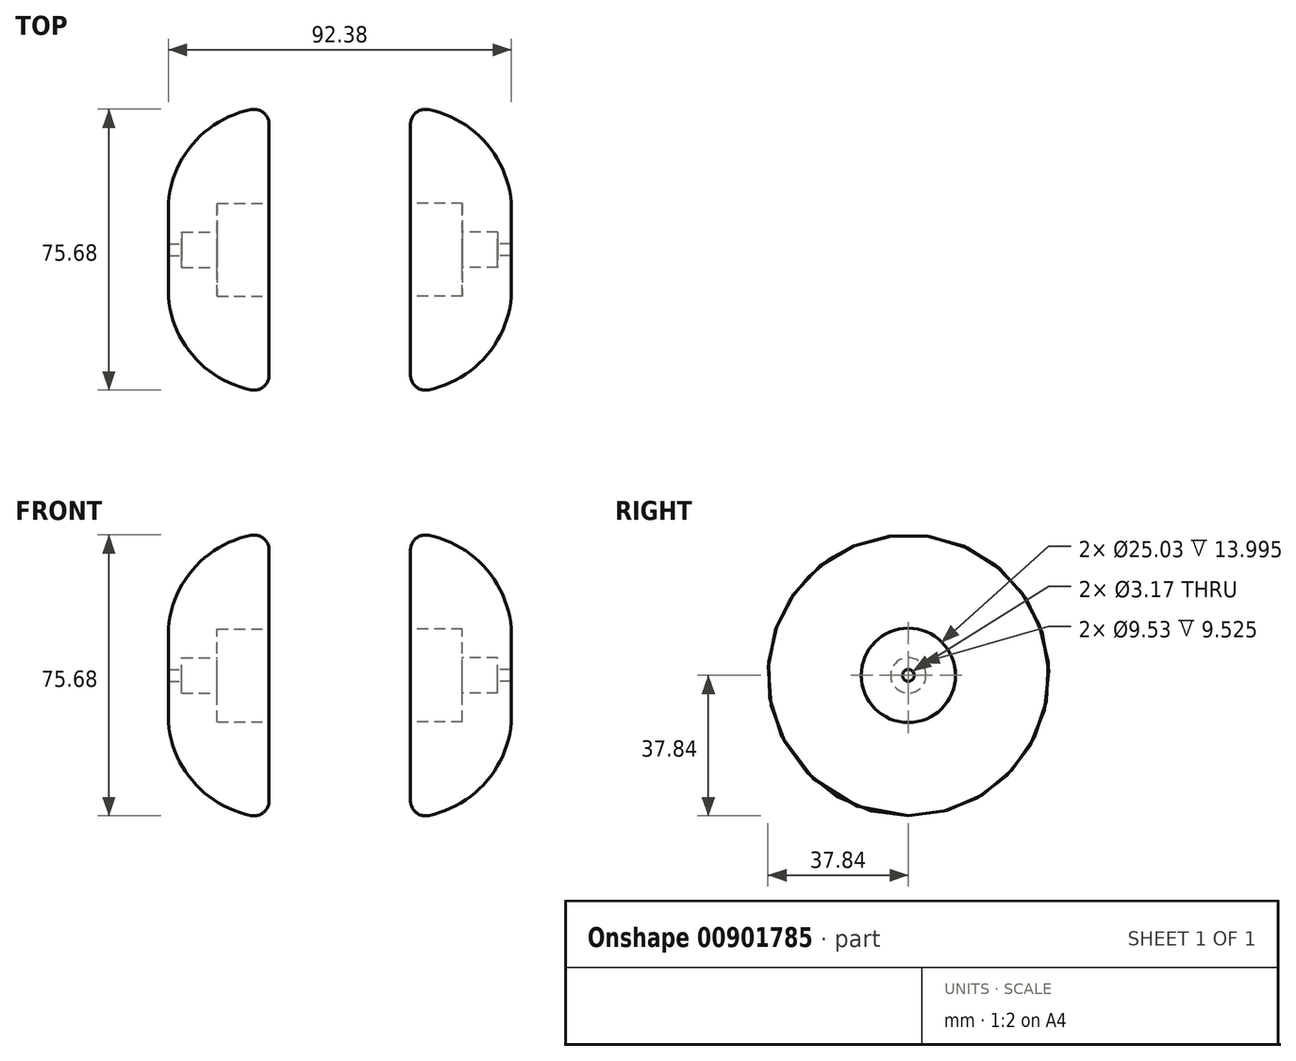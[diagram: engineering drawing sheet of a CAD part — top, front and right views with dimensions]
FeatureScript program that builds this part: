
annotation { "Feature Type Name" : "Feature", "Feature Type Description" : "" }
export const myFeature = defineFeature(function(context is Context, id is Id, definition is map)
    precondition{}
    {
        {
            var Q0;
            Q0=qCreatedBy(makeId("Front.planeOp"),FACE);
            var sketch = newSketch(context, id + "F0", { "sketchPlane" : qUnion([Q0])});
            skLineSegment(sketch, "E0", {"start": v(-80.66, 4.76) * mm, "end": v(-71.13, 4.76) * mm});
            skLineSegment(sketch, "E1", {"start": v(-71.13, 4.76) * mm, "end": v(-71.13, 12.52) * mm});
            skLineSegment(sketch, "E2", {"start": v(-80.66, 4.76) * mm, "end": v(-80.66, 1.59) * mm});
            skLineSegment(sketch, "E3", {"start": v(-71.13, 12.52) * mm, "end": v(-57.14, 12.52) * mm});
            skLineSegment(sketch, "E4", {"start": v(-57.14, 33.77) * mm, "end": v(-57.14, 12.52) * mm});
            skLineSegment(sketch, "E5", {"start": v(-84.29, 1.59) * mm, "end": v(-84.29, 12.7) * mm});
            skArc(sketch, "E6", {"start": v(-62.03, 37.75) * mm, "mid": v(-77.31, 28.92) * mm, "end": v(-84.29, 12.7) * mm});
            skPoint(sketch, "E7.visualSharp", {"position": v(-57.14, 38.32) * mm});
            skLineSegment(sketch, "E7.filletArc", {"start": v(-57.14, 38.32) * mm, "end": v(-57.14, 38.32) * mm});
            skArc(sketch, "E8.filletArc", {"start": v(-57.14, 33.77) * mm, "mid": v(-58.64, 36.92) * mm, "end": v(-62.03, 37.75) * mm});
            skLineSegment(sketch, "E9", {"start": v(-84.29, 1.59) * mm, "end": v(-80.66, 1.59) * mm});
            skLineSegment(sketch, "E10", {"start": v(-52.83, 0) * mm, "end": v(-88.66, 0) * mm, "construction": true});
            skSolve(sketch);
        }
        {
            var Q0;
            Q0=qCreatedBy(makeId("Right.planeOp"),FACE);
            cPlane(context, id + "F1", {"entities" : qUnion([Q0]), "cplaneType" : CPlaneType.OFFSET, "offset" : 38.1 * mm, "oppositeDirection" : true, "width" : 152.4 * mm, "height" : 152.4 * mm});
        }
        {
            var Q0;
            Q0=makeQuery(id+"F0.imprint","IMPRINT",FACE,{"disambiguationData":[TD([[makeQuery(id+"F0.imprint","IMPRINT",EDGE,{"derivedFrom":sQuery(id+"F0.wireOp",EDGE,"E0")}),1.0]])]});
            var Q1;
            Q1=sQuery(id+"F0.wireOp",EDGE,"E10");
            revolve(context, id + "F2", {"surfaceOperationType" : NewSurfaceOperationType.NEW, "entities" : qUnion([Q0]), "axis" : qUnion([Q1]), "revolveType" : RevolveType.FULL});
        }
        {
            var Q0;
            Q0=makeQuery(id+"F2.opRevolve","SWEPT_BODY",BODY,{"disambiguationData":[OSD([sQuery(id+"F0.wireOp",EDGE,"E0"),sQuery(id+"F0.wireOp",EDGE,"E1"),sQuery(id+"F0.wireOp",EDGE,"E2"),sQuery(id+"F0.wireOp",EDGE,"iqcDAGBw-5XQi-TltP-23vh-Z05XkJN473Cv"),sQuery(id+"F0.wireOp",EDGE,"E3"),sQuery(id+"F0.wireOp",EDGE,"E4"),sQuery(id+"F0.wireOp",EDGE,"9TaeiyYO-FVV4-SnyR-FW7R-PEr8SVDl3H7v"),sQuery(id+"F0.wireOp",EDGE,"E5"),sQuery(id+"F0.wireOp",EDGE,"E6"),sQuery(id+"F0.wireOp",EDGE,"rDqYZx4n-qk8k-G1cG-t3bS-arVaZs6p1HGe"),sQuery(id+"F0.wireOp",EDGE,"E8.filletArc")])]});
            var Q1;
            Q1=qCreatedBy(id+"F1.planeOp",FACE);
            mirror(context, id + "F3", {"entities" : qUnion([Q0]), "mirrorPlane" : qUnion([Q1])});
        }
    });
